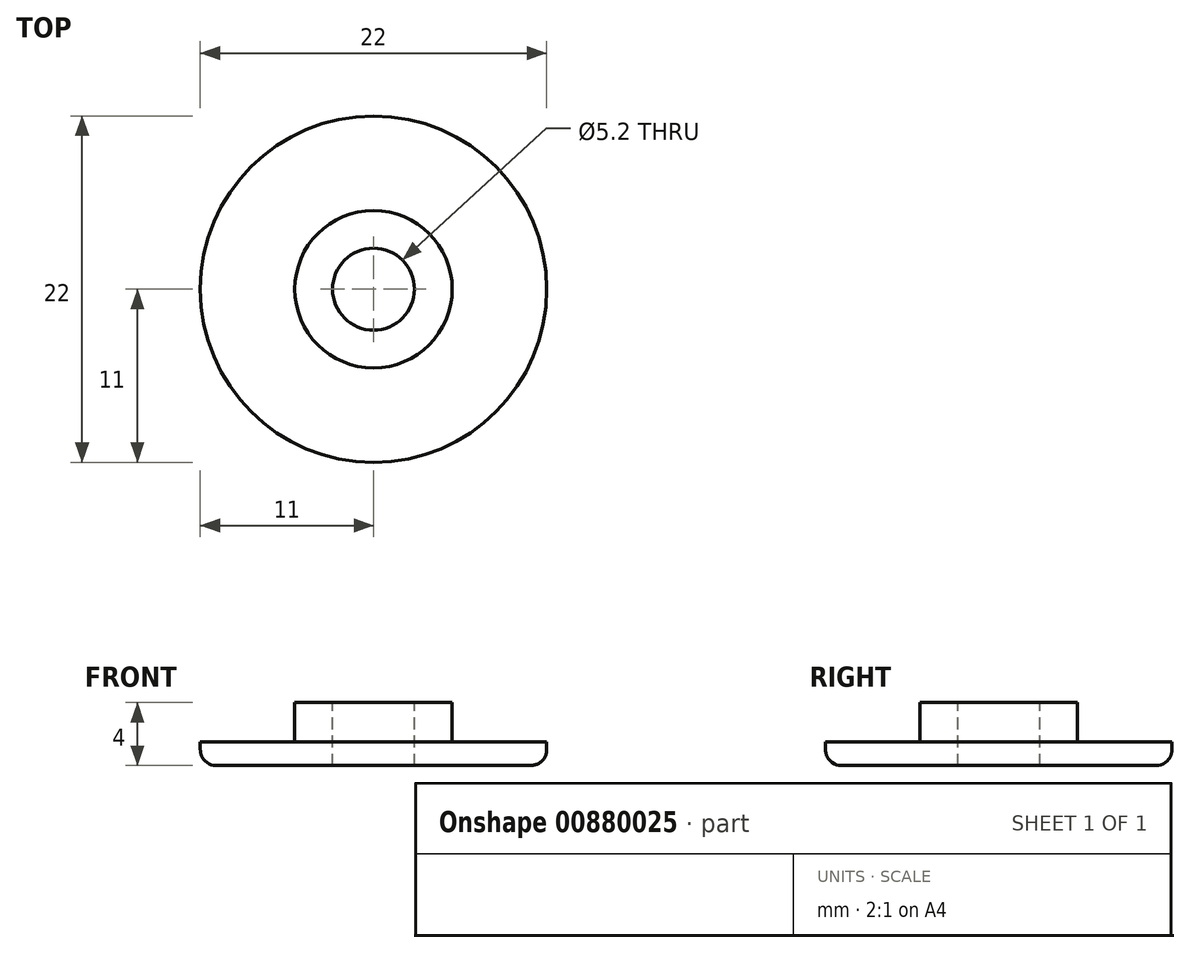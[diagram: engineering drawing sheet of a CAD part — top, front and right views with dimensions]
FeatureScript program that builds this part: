
annotation { "Feature Type Name" : "Feature", "Feature Type Description" : "" }
export const myFeature = defineFeature(function(context is Context, id is Id, definition is map)
    precondition{}
    {
        {
            var Q0;
            Q0=qCreatedBy(makeId("Top.planeOp"),FACE);
            var sketch = newSketch(context, id + "F0", { "sketchPlane" : qUnion([Q0])});
            skCircle(sketch, "E0", {"center": v(0, 0) * mm, "radius": 11 * mm});
            skSolve(sketch);
        }
        {
            var Q0;
            Q0 = qSketchRegion(id + "F0", true);
            extrude(context, id + "F1", {"entities" : qUnion([Q0]), "depth" : -1.5 * mm, "offsetDistance" : 25 * mm});
        }
        {
            var Q0;
            Q0=makeQuery(id+"F1.opExtrude","CAP_FACE",FACE,{"disambiguationData":[OSD([sQuery(id+"F0.wireOp",EDGE,"E0")])],"isStart":true});
            var sketch = newSketch(context, id + "F2", { "sketchPlane" : qUnion([Q0])});
            skCircle(sketch, "E1", {"center": v(0, 0) * mm, "radius": 5 * mm});
            skSolve(sketch);
        }
        {
            var Q0;
            Q0 = qSketchRegion(id + "F2", true);
            extrude(context, id + "F3", {"entities" : qUnion([Q0]), "operationType" : NewBodyOperationType.ADD, "depth" : 2.5 * mm, "offsetDistance" : 25 * mm});
        }
        {
            var Q0;
            Q0=makeQuery(id+"F3.opExtrude","CAP_FACE",FACE,{"disambiguationData":[OSD([sQuery(id+"F2.wireOp",EDGE,"E1")])],"isStart":false});
            var sketch = newSketch(context, id + "F4", { "sketchPlane" : qUnion([Q0])});
            skCircle(sketch, "E2", {"center": v(0, 0) * mm, "radius": 2.6 * mm});
            skSolve(sketch);
        }
        {
            var Q0;
            Q0 = qSketchRegion(id + "F4", true);
            extrude(context, id + "F5", {"entities" : qUnion([Q0]), "operationType" : NewBodyOperationType.REMOVE, "oppositeDirection" : true, "depth" : 4 * mm, "offsetDistance" : 25 * mm});
        }
        {
            var Q0;
            Q0=makeQuery(id+"F1.opExtrude","CAP_EDGE",EDGE,{"disambiguationData":[OSD([sQuery(id+"F0.wireOp",EDGE,"E0")])],"isStart":false});
            fillet(context, id + "F6", {"entities" : qUnion([Q0]), "radius" : 1 * mm, "tangentPropagation" : true, "allowEdgeOverflow" : false});
        }
    });
